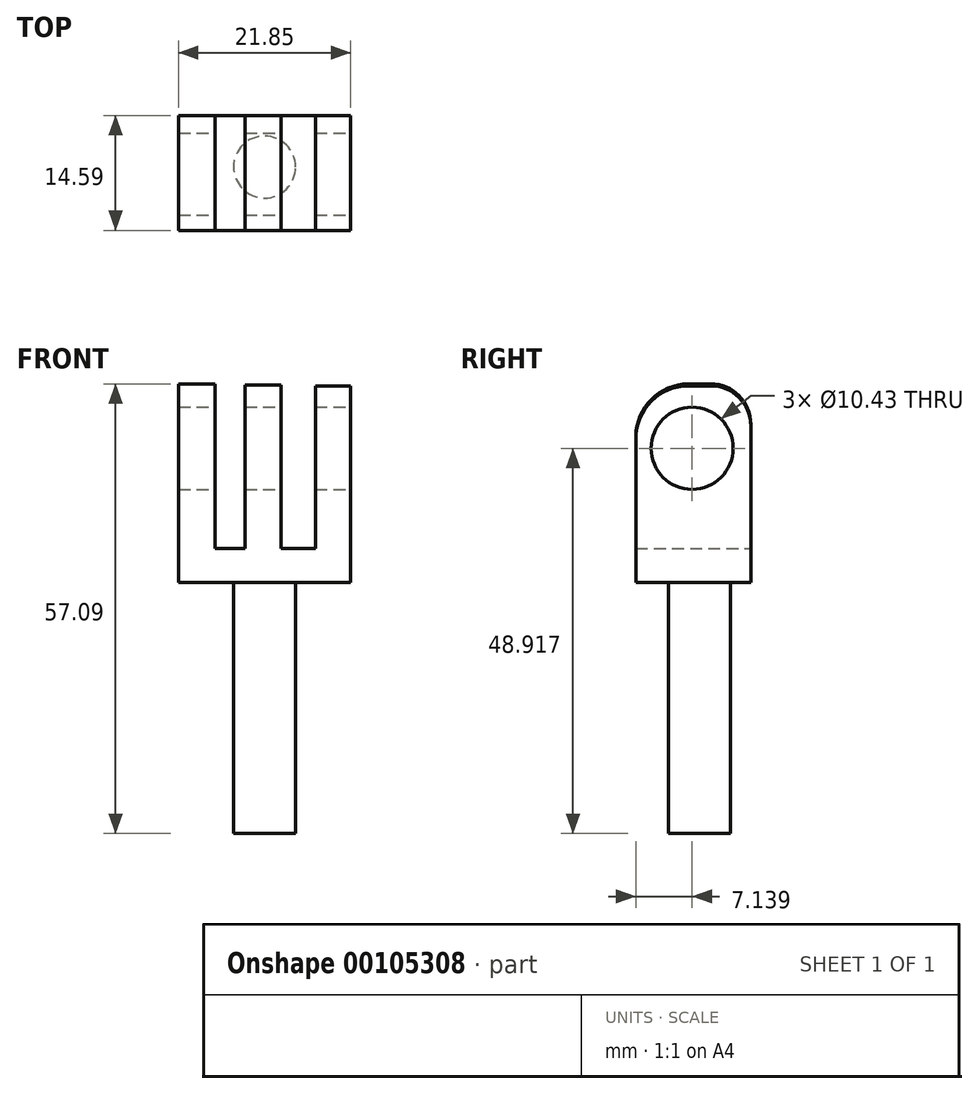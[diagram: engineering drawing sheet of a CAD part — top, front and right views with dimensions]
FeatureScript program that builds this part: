
annotation { "Feature Type Name" : "Feature", "Feature Type Description" : "" }
export const myFeature = defineFeature(function(context is Context, id is Id, definition is map)
    precondition{}
    {
        {
            var Q0;
            Q0=qCreatedBy(makeId("Front.planeOp"),FACE);
            var sketch = newSketch(context, id + "F0", { "sketchPlane" : qUnion([Q0])});
            skLineSegment(sketch, "E0.bottom", {"start": v(-7.54, -10.1) * mm, "end": v(-2.93, -10.1) * mm});
            skLineSegment(sketch, "E0.top", {"start": v(-7.54, 15.15) * mm, "end": v(-2.93, 15.15) * mm});
            skLineSegment(sketch, "E0.left", {"start": v(-7.54, -10.1) * mm, "end": v(-7.54, 15.15) * mm});
            skLineSegment(sketch, "E0.right", {"start": v(-2.93, -10.1) * mm, "end": v(-2.93, 15.15) * mm});
            skLineSegment(sketch, "E1.bottom", {"start": v(0.92, -10.1) * mm, "end": v(5.49, -10.1) * mm});
            skLineSegment(sketch, "E1.top", {"start": v(0.92, 15.03) * mm, "end": v(5.49, 15.03) * mm});
            skLineSegment(sketch, "E1.left", {"start": v(0.92, -10.1) * mm, "end": v(0.92, 15.03) * mm});
            skLineSegment(sketch, "E1.right", {"start": v(5.49, -10.1) * mm, "end": v(5.49, 15.03) * mm});
            skLineSegment(sketch, "E2.bottom", {"start": v(9.84, -10.1) * mm, "end": v(14.3, -10.1) * mm});
            skLineSegment(sketch, "E2.top", {"start": v(9.84, 14.91) * mm, "end": v(14.3, 14.91) * mm});
            skLineSegment(sketch, "E2.left", {"start": v(9.84, -10.1) * mm, "end": v(9.84, 14.91) * mm});
            skLineSegment(sketch, "E2.right", {"start": v(14.3, -10.1) * mm, "end": v(14.3, 14.91) * mm});
            skLineSegment(sketch, "E3.bottom", {"start": v(-7.54, -5.76) * mm, "end": v(14.3, -5.76) * mm});
            skLineSegment(sketch, "E3.top", {"start": v(-7.54, -10.1) * mm, "end": v(14.3, -10.1) * mm});
            skLineSegment(sketch, "E3.left", {"start": v(-7.54, -5.76) * mm, "end": v(-7.54, -10.1) * mm});
            skLineSegment(sketch, "E3.right", {"start": v(14.3, -5.76) * mm, "end": v(14.3, -10.1) * mm});
            skSolve(sketch);
        }
        {
            var Q0;
            Q0 = qSketchRegion(id + "F0", true);
            extrude(context, id + "F1", {"entities" : qUnion([Q0]), "depth" : 14.6 * mm});
        }
        {
            var Q0;
            Q0=makeQuery(id+"F1.opExtrude","SWEPT_FACE",FACE,{"disambiguationData":[OSD([sQuery(id+"F0.wireOp",EDGE,"E2.right"),sQuery(id+"F0.wireOp",EDGE,"E3.right")])]});
            var sketch = newSketch(context, id + "F2", { "sketchPlane" : qUnion([Q0])});
            skCircle(sketch, "E4", {"center": v(-7.45, 6.98) * mm, "radius": 5.22 * mm});
            skSolve(sketch);
        }
        {
            var Q0;
            Q0 = qSketchRegion(id + "F2", true);
            extrude(context, id + "F3", {"entities" : qUnion([Q0]), "operationType" : NewBodyOperationType.REMOVE, "oppositeDirection" : true, "depth" : 26.43 * mm});
        }
        {
            var Q0;
            Q0=makeQuery(id+"F1.opExtrude","CAP_EDGE",EDGE,{"disambiguationData":[OSD([sQuery(id+"F0.wireOp",EDGE,"E0.top")])],"isStart":false});
            var Q1;
            Q1=makeQuery(id+"F1.opExtrude","CAP_EDGE",EDGE,{"disambiguationData":[OSD([sQuery(id+"F0.wireOp",EDGE,"E1.top")])],"isStart":false});
            var Q2;
            Q2=makeQuery(id+"F1.opExtrude","CAP_EDGE",EDGE,{"disambiguationData":[OSD([sQuery(id+"F0.wireOp",EDGE,"E2.top")])],"isStart":false});
            fillet(context, id + "F4", {"entities" : qUnion([Q0, Q1, Q2]), "radius" : 6.67 * mm, "tangentPropagation" : true, "allowEdgeOverflow" : false});
        }
        {
            var Q0;
            Q0=makeQuery(id+"F1.opExtrude","CAP_EDGE",EDGE,{"disambiguationData":[OSD([sQuery(id+"F0.wireOp",EDGE,"E2.top")])],"isStart":true});
            var Q1;
            Q1=makeQuery(id+"F1.opExtrude","CAP_EDGE",EDGE,{"disambiguationData":[OSD([sQuery(id+"F0.wireOp",EDGE,"E1.top")])],"isStart":true});
            var Q2;
            Q2=makeQuery(id+"F1.opExtrude","CAP_EDGE",EDGE,{"disambiguationData":[OSD([sQuery(id+"F0.wireOp",EDGE,"E0.top")])],"isStart":true});
            fillet(context, id + "F5", {"entities" : qUnion([Q0, Q1, Q2]), "radius" : 5.08 * mm, "tangentPropagation" : true, "allowEdgeOverflow" : false});
        }
        {
            var Q0;
            Q0=makeQuery(id+"F1.opExtrude","SWEPT_FACE",FACE,{"disambiguationData":[OSD([sQuery(id+"F0.wireOp",EDGE,"E3.top")])]});
            var sketch = newSketch(context, id + "F6", { "sketchPlane" : qUnion([Q0])});
            skCircle(sketch, "E5", {"center": v(3.39, 6.53) * mm, "radius": 3.94 * mm});
            skPoint(sketch, "E5.centerSnap0", {"position": v(3.39, 14.59) * mm});
            skSolve(sketch);
        }
        {
            var Q0;
            Q0=makeQuery(id+"F6.imprint","IMPRINT",FACE,{"disambiguationData":[TD([[makeQuery(id+"F6.imprint","IMPRINT",EDGE,{"derivedFrom":sQuery(id+"F6.wireOp",EDGE,"E5")}),1.0]])]});
            extrude(context, id + "F7", {"entities" : qUnion([Q0]), "operationType" : NewBodyOperationType.ADD, "depth" : 31.84 * mm});
        }
    });
